# Revit family: NAU_Naughtone_Stng_Polly_4Leg1
name_source: partatom
category: Furniture
revit_build: Autodesk Revit 2018 (Build: 20170223_1515(x64)
units: mm (PartAtom-declared; Revit-internal decimal feet)

## family parameters
Always vertical = Yes
Cut with Voids When Loaded = No
OmniClass Number = 23.40.20.00
OmniClass Title = General Furniture and Specialties
Room Calculation Point = No
Shared = Yes
Work Plane-Based = No

## types (2) — shared parameters
Assembly Code = E2020200
AssetType = Movable
BIMObjectName = NAU_Naughtone_Seating_Polly_4Leg
Category = Pr_40_50_12 : Chairs, seats and benches
Color = Various
DurationUnit = year
Finish = Plastic Shell in 8 RAL colours
IfcExportAs = IfcFurnishingElementType
IfcExportType = CHAIR
Keynote = Pr_40_50_12
MainColor = Various
ManufacturerAddress = Knaresborough Tech Park, Manse Lane, Knaresborough, HG5 8LF
ManufacturerName = Naughtone
ManufacturerURL = www.naughtone.com
NBSDescription = Seating
NBSReference = 45-35-72/352
Name = Seating_Polly_4Leg_Naughtone
NominalLength = 530 mm  [stored 1.73885 ft]
ProductInformation = www.naughtone.com/portfolio-view/polly
ReplacementCost = 0.00
Revision = 1
Shape = Rectangular
SustainabilityPerformance = FISP certified. ISO 14001. SCS indoor advantage gold
URL = www.naughtone.com
Uniclass2015Code = Pr_40_50_12
Uniclass2015Title = Chairs, seats and benches
Version = 1
WarrantyDescription = Request warranty information from naughtone
WarrantyDurationLabor = 7
WarrantyDurationParts = 7
WarrantyDurationUnit = year

## per-type parameters (varying)
| type | Description | IsPOLLYCHB4L | IsPOLLYCHBDL | Material | ModelReference | NominalHeight | NominalWidth | Size |
| POLLYCHBDL | Polly Chair Dowel Base | No | Yes | Legs in Oak or Walnut | Polly Chair Dowel Base | 795 mm  [stored 2.60827 ft] | 505 mm  [stored 1.65682 ft] | 530 x 505 x 795mm |
| POLLYCHB4L | Polly 4 Leg Chair | Yes | No | Metal/plastic | Polly 4 Leg Chair | 785 mm | 513 mm  [stored 1.68307 ft] | 530 x 513 x 785mm |

note: column(s) folded — value = type name in every type: Model, ModelNumber

note: [stored X ft] marks values corroborated as IEEE doubles in the binary element streams (Revit-internal decimal feet)

## geometry (parser evidence)
native form markers: Sweep x4
no freeform markers — native parametric forms only
